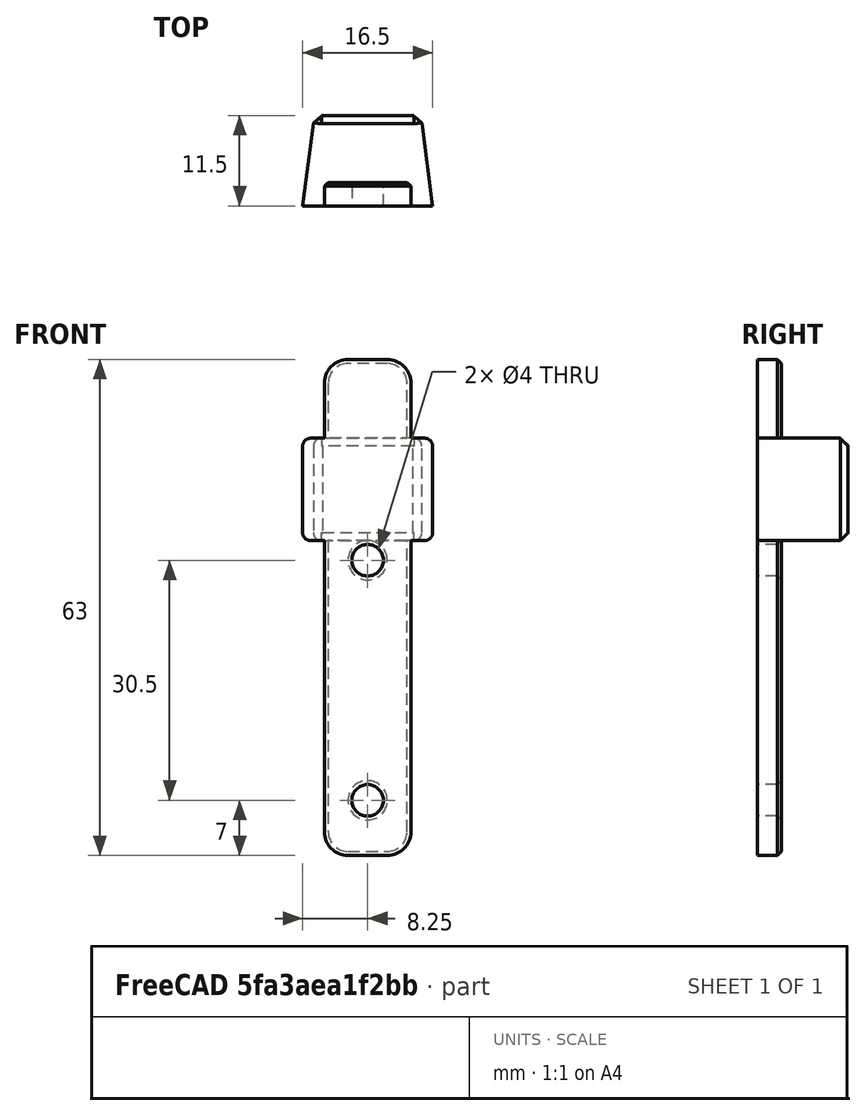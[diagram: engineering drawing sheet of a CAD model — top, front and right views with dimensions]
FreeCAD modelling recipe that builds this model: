
FCSTD DOCUMENT  (FreeCAD 1.0R39319 (Git))
Label: Decathlon_Seat_Footrest_fix
License: All rights reserved
LicenseURL: https://en.wikipedia.org/wiki/All_rights_reserved
objects: PartDesign::Chamfer×4, Sketcher::SketchObject×3, PartDesign::Pad×3, PartDesign::Fillet×3, PartDesign::Body×1
note: 37 computed .brp shape members not serialized (recipe doc carries the construction recipe); baked Part::Feature solids carry a one-line shape summary decoded from their .brp

FEATURE [Sketcher::SketchObject] Sketch
  ArcFitTolerance = 1e-06
  AttachmentSupport = -> [XY_Plane]
  FullyConstrained = true
  MakeInternals = false
  MapMode = 5
  expr: Constraints[3] = 13.5 / 2
  expr: Constraints[4] = 16.5 / 2
  sketch-geometry (6):
    g0: LineSegment StartX=0 StartY=11.5 StartZ=0 EndX=6.75 EndY=11.5 EndZ=0
    g1: LineSegment StartX=6.75 StartY=11.5 StartZ=0 EndX=8.25 EndY=0 EndZ=0
    g2: LineSegment StartX=8.25 StartY=0 StartZ=0 EndX=0 EndY=0 EndZ=0
    g3: LineSegment StartX=0 StartY=11.5 StartZ=0 EndX=-6.75 EndY=11.5 EndZ=0
    g4: LineSegment StartX=-6.75 StartY=11.5 StartZ=0 EndX=-8.25 EndY=0 EndZ=0
    g5: LineSegment StartX=-8.25 StartY=0 StartZ=0 EndX=0 EndY=0 EndZ=0
  constraints (17):
    c: Coincident(g0,g1)
    c: Coincident(g1,g2)
    c: Horizontal(g2)
    c: DistanceX(g0,g0) = 6.75
    c: DistanceX(g2,g2) = 8.25
    c: DistanceY(g0,g2) = -11.5
    c: Coincident(g3,g4)
    c: Coincident(g4,g5)
    c: Horizontal(g5)
    c: Coincident(g5,g2)
    c: Equal(g5,g2)
    c: Equal(g3,g0)
    c: Coincident(g3,g0)
    c: Horizontal(g3)
    c: PointOnObject(g0,g-2)
    c: Coincident(g2,g-1)
    c: Horizontal(g0)
FEATURE [PartDesign::Pad] Pad
  Direction = (0,0,1)
  Length = 13
  Length2 = 10
  Profile = -> Sketch
  ReferenceAxis = -> Sketch [N_Axis]
  Refine = true
  Suppressed = false
  Type = 0
FEATURE [Sketcher::SketchObject] Sketch001
  ArcFitTolerance = 1e-06
  AttachmentSupport = -> [XZ_Plane]
  FullyConstrained = true
  MakeInternals = false
  MapMode = 5
  Placement = pos=(0,0,0) rot=(1,0,0;1.5708rad)
  sketch-geometry (7):
    g0: LineSegment StartX=-5.5 StartY=-40 StartZ=0 EndX=5.5 EndY=-40 EndZ=0
    g1: LineSegment StartX=5.5 StartY=-40 StartZ=0 EndX=5.5 EndY=0 EndZ=0
    g2: LineSegment StartX=5.5 StartY=0 StartZ=0 EndX=-5.5 EndY=0 EndZ=0
    g3: LineSegment StartX=-5.5 StartY=0 StartZ=0 EndX=-5.5 EndY=-40 EndZ=0
    g4: GeomPoint [constr] X=0 Y=-20 Z=0
    g5: Circle CenterX=0 CenterY=-2.5 CenterZ=0 NormalX=0 NormalY=0 NormalZ=1 AngleXU=0 Radius=2
    g6: Circle CenterX=0 CenterY=-33 CenterZ=0 NormalX=0 NormalY=0 NormalZ=1 AngleXU=0 Radius=2
  constraints (19):
    c: Coincident(g0,g1)
    c: Coincident(g1,g2)
    c: Coincident(g2,g3)
    c: Coincident(g3,g0)
    c: Horizontal(g0)
    c: Horizontal(g2)
    c: Vertical(g1)
    c: Vertical(g3)
    c: Symmetric(g2,g0,g4)
    c: PointOnObject(g4,g-2)
    c: PointOnObject(g1,g-1)
    c: DistanceY(g3,g3) = 40
    c: DistanceX(g0,g0) = 11
    c: PointOnObject(g5,g-2)
    c: PointOnObject(g6,g-2)
    c: Equal(g6,g5)
    c: Diameter(g5) = 4
    c: DistanceY(g5,g-1) = 2.5
    c: DistanceY(g0,g6) = 7
FEATURE [PartDesign::Pad] Pad001
  BaseFeature = -> Pad
  Direction = (0,-1,2e-16)
  Length = 3
  Length2 = 10
  Profile = -> Sketch001
  ReferenceAxis = -> Sketch001 [N_Axis]
  Refine = true
  Reversed = true
  Suppressed = false
  Type = 0
FEATURE [PartDesign::Fillet] Fillet
  Base = -> Pad001 [Edge13,Edge15,Edge3,Edge4]
  BaseFeature = -> Pad001
  Radius = 1
  Refine = true
  SupportTransform = false
  Suppressed = false
  UseAllEdges = false
FEATURE [PartDesign::Chamfer] Chamfer
  Angle = 45
  Base = -> Fillet [Face2]
  BaseFeature = -> Fillet
  ChamferType = 0
  FlipDirection = false
  Refine = true
  Size = 1
  Size2 = 1
  SupportTransform = false
  Suppressed = false
  UseAllEdges = false
FEATURE [PartDesign::Fillet] Fillet001
  Base = -> Chamfer [Edge41,Edge45]
  BaseFeature = -> Chamfer
  Radius = 3
  Refine = true
  SupportTransform = false
  Suppressed = false
  UseAllEdges = false
FEATURE [PartDesign::Chamfer] Chamfer001
  Angle = 45
  Base = -> Fillet001 [Edge35]
  BaseFeature = -> Fillet001
  ChamferType = 0
  FlipDirection = false
  Refine = true
  Size = 0.5
  Size2 = 1
  SupportTransform = false
  Suppressed = false
  UseAllEdges = false
FEATURE [PartDesign::Chamfer] Chamfer002
  Angle = 45
  Base = -> Chamfer001 [Edge38,Edge39]
  BaseFeature = -> Chamfer001
  ChamferType = 0
  FlipDirection = false
  Refine = true
  Size = 0.5
  Size2 = 1
  SupportTransform = false
  Suppressed = false
  UseAllEdges = false
FEATURE [Sketcher::SketchObject] Sketch002
  ArcFitTolerance = 1e-06
  AttachmentSupport = -> [XZ_Plane]
  ExternalGeometry = -> [Chamfer002]
  FullyConstrained = true
  MakeInternals = false
  MapMode = 5
  Placement = pos=(0,0,0) rot=(1,0,0;1.5708rad)
  sketch-geometry (5):
    g0: LineSegment StartX=-5.5 StartY=23 StartZ=0 EndX=-5.5 EndY=13 EndZ=0
    g1: LineSegment StartX=-5.5 StartY=13 StartZ=0 EndX=5.5 EndY=13 EndZ=0
    g2: LineSegment StartX=5.5 StartY=13 StartZ=0 EndX=5.5 EndY=23 EndZ=0
    g3: LineSegment StartX=5.5 StartY=23 StartZ=0 EndX=-5.5 EndY=23 EndZ=0
    g4: GeomPoint [constr] X=1e-16 Y=18 Z=0
  constraints (13):
    c: Coincident(g0,g1)
    c: Coincident(g1,g2)
    c: Coincident(g2,g3)
    c: Coincident(g3,g0)
    c: Vertical(g0)
    c: Vertical(g2)
    c: Horizontal(g1)
    c: Horizontal(g3)
    c: Symmetric(g2,g0,g4)
    c: PointOnObject(g4,g-2)
    c: PointOnObject(g1,g-3)
    c: DistanceY(g2,g2) = 10
    c: DistanceX(g3,g3) = 11
FEATURE [PartDesign::Pad] Pad002
  BaseFeature = -> Chamfer002
  Direction = (0,-1,2e-16)
  Length = 3
  Length2 = 10
  Profile = -> Sketch002
  ReferenceAxis = -> Sketch002 [N_Axis]
  Refine = true
  Reversed = true
  Suppressed = false
  Type = 0
FEATURE [PartDesign::Fillet] Fillet002
  Base = -> Pad002 [Edge88,Edge83]
  BaseFeature = -> Pad002
  Radius = 3
  Refine = true
  SupportTransform = false
  Suppressed = false
  UseAllEdges = false
FEATURE [PartDesign::Chamfer] Chamfer003
  Angle = 45
  Base = -> Fillet002 [Edge4]
  BaseFeature = -> Fillet002
  ChamferType = 0
  FlipDirection = false
  Refine = true
  Size = 0.5
  Size2 = 1
  SupportTransform = false
  Suppressed = false
  UseAllEdges = false
FEATURE [PartDesign::Body] Body
  AllowCompound = false
  Group = -> [Sketch,Pad,Sketch001,Pad001,Fillet,Chamfer,Fillet001,Chamfer001,Chamfer002,Sketch002,Pad002,Fillet002,Chamfer003]
  Origin = -> Origin
  Tip = -> Chamfer003
